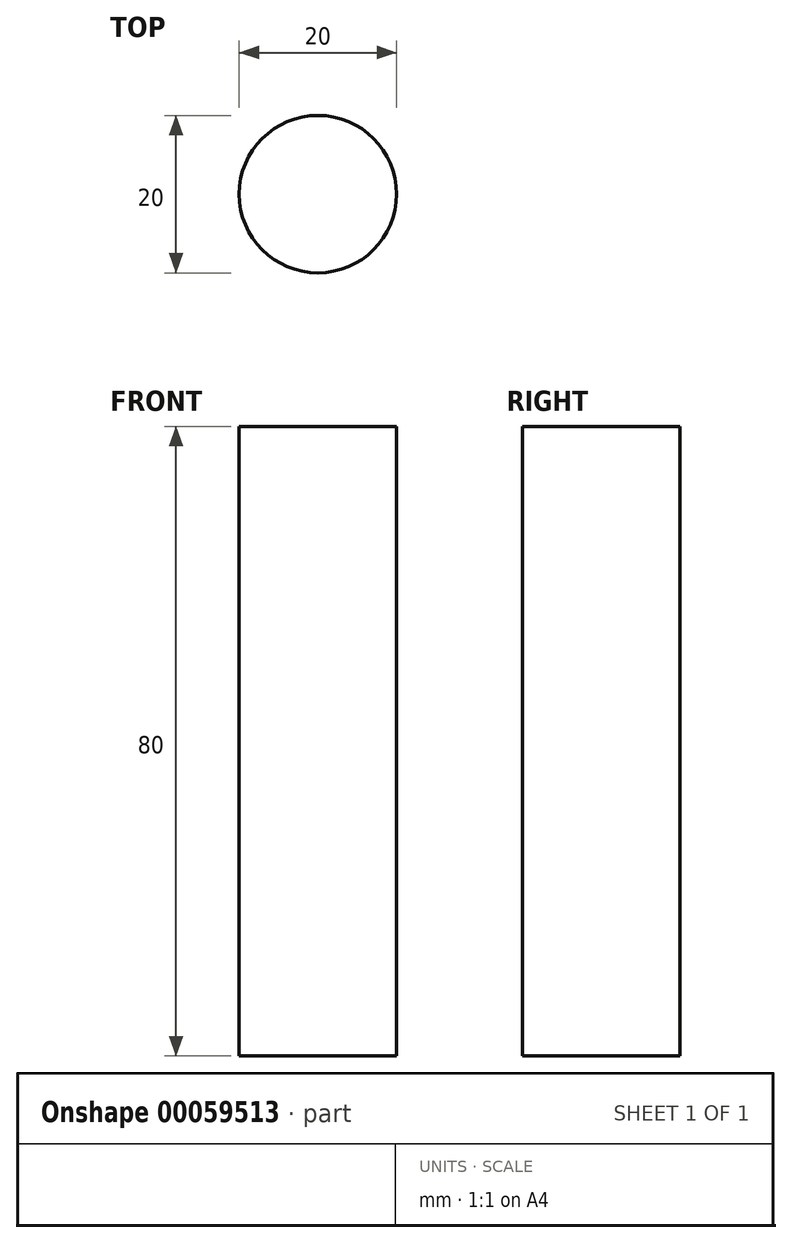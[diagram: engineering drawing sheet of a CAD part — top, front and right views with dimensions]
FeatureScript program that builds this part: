
annotation { "Feature Type Name" : "Feature", "Feature Type Description" : "" }
export const myFeature = defineFeature(function(context is Context, id is Id, definition is map)
    precondition{}
    {
        {
            var Q0;
            Q0=qCreatedBy(makeId("Top.planeOp"),FACE);
            var sketch = newSketch(context, id + "F0", { "sketchPlane" : qUnion([Q0])});
            skCircle(sketch, "E0", {"center": v(0, 0) * mm, "radius": 10 * mm});
            skSolve(sketch);
        }
        {
            var Q0;
            Q0=makeQuery(id+"F0.imprint","IMPRINT",FACE,{"disambiguationData":[TD([[makeQuery(id+"F0.imprint","IMPRINT",EDGE,{"derivedFrom":sQuery(id+"F0.wireOp",EDGE,"E0")}),1.0]])]});
            extrude(context, id + "F1", {"entities" : qUnion([Q0]), "depth" : 80 * mm});
        }
    });
